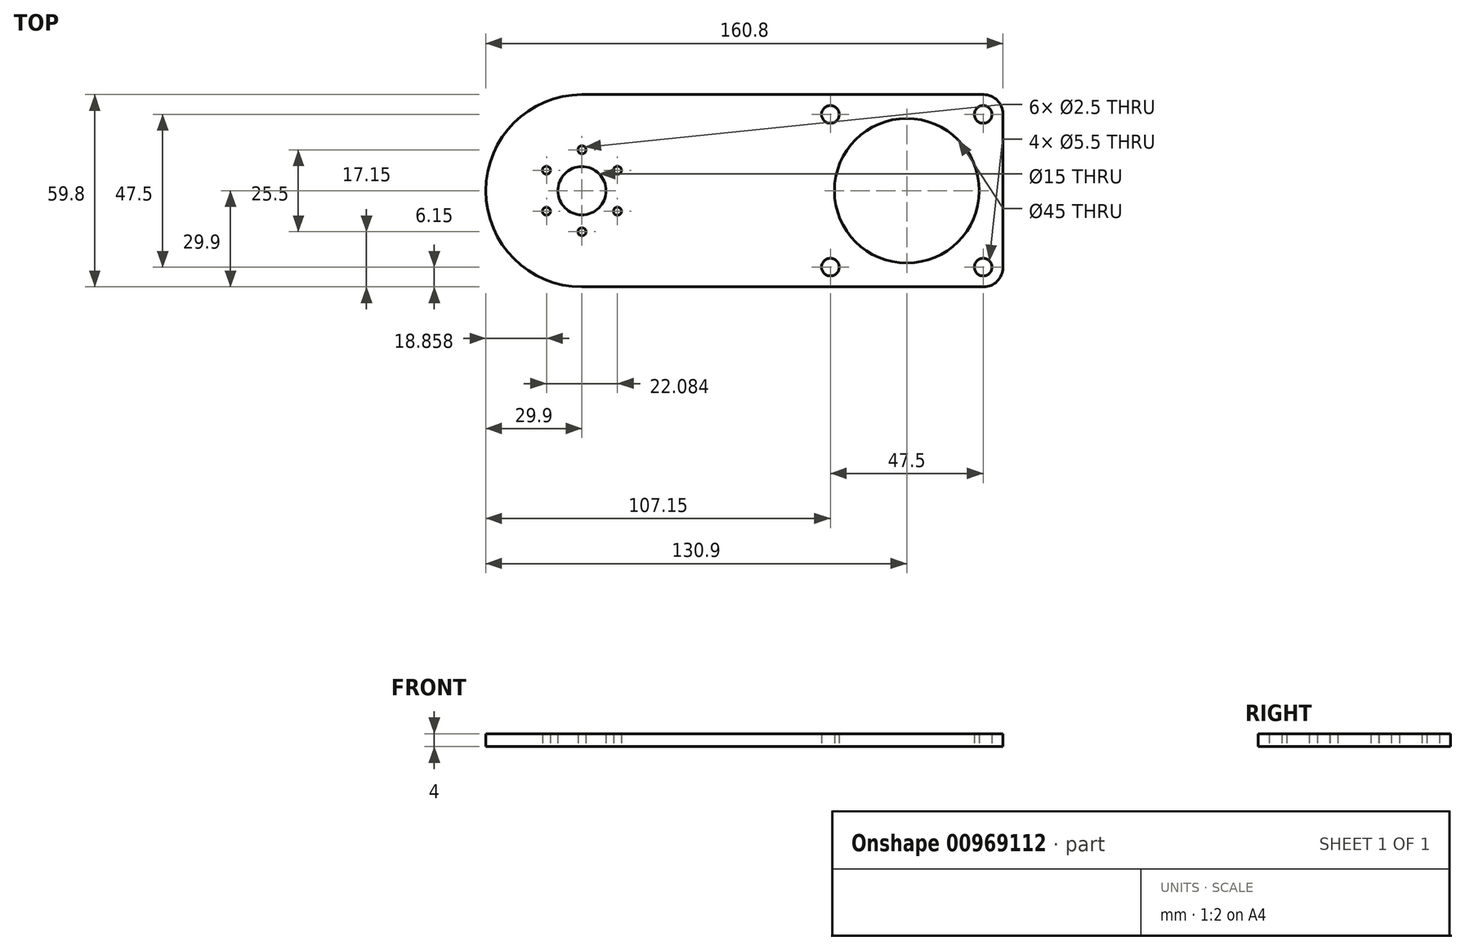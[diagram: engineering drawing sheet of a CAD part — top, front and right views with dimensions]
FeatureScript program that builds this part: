
annotation { "Feature Type Name" : "Feature", "Feature Type Description" : "" }
export const myFeature = defineFeature(function(context is Context, id is Id, definition is map)
    precondition{}
    {
        {
            var Q0;
            Q0=qCreatedBy(makeId("Top.planeOp"),FACE);
            var sketch = newSketch(context, id + "F0", { "sketchPlane" : qUnion([Q0])});
            skLineSegment(sketch, "E0.bottom", {"start": v(-101, 29.9) * mm, "end": v(23.9, 29.9) * mm});
            skLineSegment(sketch, "E0.top", {"start": v(-101, -29.9) * mm, "end": v(23.9, -29.9) * mm});
            skLineSegment(sketch, "E0.left", {"start": v(-130.9, 0) * mm, "end": v(-130.9, 0) * mm});
            skLineSegment(sketch, "E0.right", {"start": v(29.9, 23.9) * mm, "end": v(29.9, -23.9) * mm});
            skCircle(sketch, "E1", {"center": v(23.75, 23.75) * mm, "radius": 2.75 * mm});
            skCircle(sketch, "E2", {"center": v(23.75, -23.75) * mm, "radius": 2.75 * mm});
            skLineSegment(sketch, "E3", {"start": v(23.75, 23.75) * mm, "end": v(23.75, -23.75) * mm, "construction": true});
            skLineSegment(sketch, "E4", {"start": v(23.75, 23.75) * mm, "end": v(29.9, 23.75) * mm, "construction": true});
            skLineSegment(sketch, "E5", {"start": v(23.75, 23.75) * mm, "end": v(23.75, 29.9) * mm, "construction": true});
            skCircle(sketch, "E6", {"center": v(-23.75, 23.75) * mm, "radius": 2.75 * mm});
            skCircle(sketch, "E7", {"center": v(-23.75, -23.75) * mm, "radius": 2.75 * mm});
            skLineSegment(sketch, "E8", {"start": v(-23.75, 23.75) * mm, "end": v(-23.75, 29.9) * mm, "construction": true});
            skLineSegment(sketch, "E9", {"start": v(-23.75, -23.75) * mm, "end": v(-23.75, -29.9) * mm, "construction": true});
            skLineSegment(sketch, "E10", {"start": v(-23.75, 23.75) * mm, "end": v(-23.75, -23.75) * mm, "construction": true});
            skLineSegment(sketch, "E11", {"start": v(-23.75, 23.75) * mm, "end": v(23.75, 23.75) * mm, "construction": true});
            skCircle(sketch, "E12", {"center": v(0, 0) * mm, "radius": 22.5 * mm});
            skLineSegment(sketch, "E13", {"start": v(0, 0) * mm, "end": v(23.75, 23.75) * mm, "construction": true});
            skLineSegment(sketch, "E14", {"start": v(0, 0) * mm, "end": v(-23.75, 23.75) * mm, "construction": true});
            skPoint(sketch, "E15.visualSharp", {"position": v(29.9, 29.9) * mm});
            skArc(sketch, "E15.filletArc", {"start": v(29.9, 23.9) * mm, "mid": v(28.14, 28.14) * mm, "end": v(23.9, 29.9) * mm});
            skPoint(sketch, "E16.visualSharp", {"position": v(29.9, -29.9) * mm});
            skArc(sketch, "E16.filletArc", {"start": v(23.9, -29.9) * mm, "mid": v(28.14, -28.14) * mm, "end": v(29.9, -23.9) * mm});
            skCircle(sketch, "E17", {"center": v(-101, 0) * mm, "radius": 7.5 * mm});
            skCircle(sketch, "E18", {"center": v(-89.96, 6.37) * mm, "radius": 1.25 * mm});
            skCircle(sketch, "E19", {"center": v(-89.96, -6.38) * mm, "radius": 1.25 * mm});
            skCircle(sketch, "E20", {"center": v(-101, -12.75) * mm, "radius": 1.25 * mm});
            skCircle(sketch, "E21", {"center": v(-112.04, -6.37) * mm, "radius": 1.25 * mm});
            skCircle(sketch, "E22", {"center": v(-112.04, 6.37) * mm, "radius": 1.25 * mm});
            skCircle(sketch, "E23", {"center": v(-101, 12.75) * mm, "radius": 1.25 * mm});
            skCircle(sketch, "E24.cCircle", {"center": v(-101, 0) * mm, "radius": 12.75 * mm, "construction": true});
            skLineSegment(sketch, "E24.0", {"start": v(-89.96, 6.37) * mm, "end": v(-89.96, -6.38) * mm, "construction": true});
            skLineSegment(sketch, "E24.1", {"start": v(-89.96, -6.37) * mm, "end": v(-101, -12.75) * mm, "construction": true});
            skLineSegment(sketch, "E24.2", {"start": v(-101, -12.75) * mm, "end": v(-112.04, -6.37) * mm, "construction": true});
            skLineSegment(sketch, "E24.3", {"start": v(-112.04, -6.37) * mm, "end": v(-112.04, 6.37) * mm, "construction": true});
            skLineSegment(sketch, "E24.4", {"start": v(-112.04, 6.37) * mm, "end": v(-101, 12.75) * mm, "construction": true});
            skLineSegment(sketch, "E24.5", {"start": v(-101, 12.75) * mm, "end": v(-89.96, 6.37) * mm, "construction": true});
            skLineSegment(sketch, "E25", {"start": v(-113.75, 0) * mm, "end": v(-130.9, 0) * mm, "construction": true});
            skLineSegment(sketch, "E26", {"start": v(-101, 12.75) * mm, "end": v(-101, 29.9) * mm, "construction": true});
            skLineSegment(sketch, "E27", {"start": v(-113.75, 0) * mm, "end": v(29.9, 0) * mm, "construction": true});
            skLineSegment(sketch, "E28", {"start": v(-101, 12.75) * mm, "end": v(-101, -29.9) * mm, "construction": true});
            skPoint(sketch, "E29.visualSharp", {"position": v(-130.9, 29.9) * mm});
            skArc(sketch, "E29.filletArc", {"start": v(-101, 29.9) * mm, "mid": v(-122.14, 21.14) * mm, "end": v(-130.9, 0) * mm});
            skPoint(sketch, "E30.visualSharp", {"position": v(-130.9, -29.9) * mm});
            skArc(sketch, "E30.filletArc", {"start": v(-130.9, 0) * mm, "mid": v(-122.14, -21.14) * mm, "end": v(-101, -29.9) * mm});
            skSolve(sketch);
        }
        {
            var Q0;
            Q0 = qSketchRegion(id + "F0", true);
            extrude(context, id + "F1", {"entities" : qUnion([Q0]), "depth" : 4 * mm, "offsetDistance" : 25 * mm});
        }
    });
